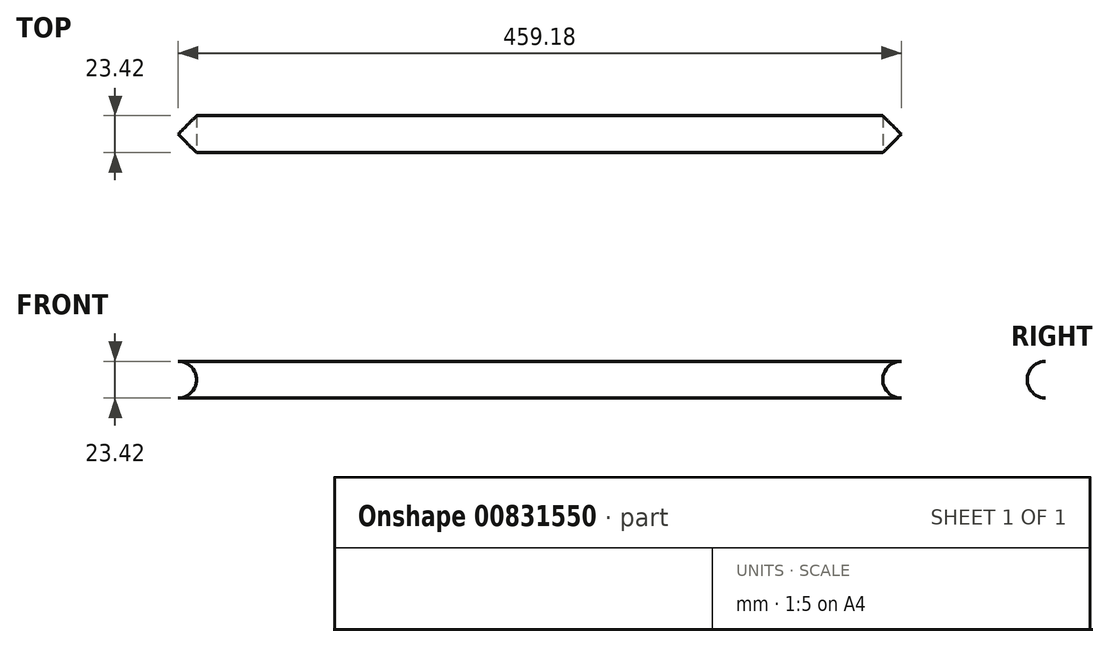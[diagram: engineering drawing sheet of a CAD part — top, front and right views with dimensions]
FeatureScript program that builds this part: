
annotation { "Feature Type Name" : "Feature", "Feature Type Description" : "" }
export const myFeature = defineFeature(function(context is Context, id is Id, definition is map)
    precondition{}
    {
        {
            var Q0;
            Q0=qCreatedBy(makeId("Right.planeOp"),FACE);
            var sketch = newSketch(context, id + "F0", { "sketchPlane" : qUnion([Q0])});
            skCircle(sketch, "E0", {"center": v(0, 0) * mm, "radius": 11.7 * mm});
            skSolve(sketch);
        }
        {
            var Q0;
            Q0=makeQuery(id+"F0.imprint","IMPRINT",FACE,{"disambiguationData":[TD([[makeQuery(id+"F0.imprint","IMPRINT",EDGE,{"derivedFrom":sQuery(id+"F0.wireOp",EDGE,"E0")}),1.0]])]});
            extrude(context, id + "F1", {"entities" : qUnion([Q0]), "depth" : 459.18 * mm, "offsetDistance" : 25.4 * mm});
        }
        {
            var Q0;
            Q0=qCreatedBy(makeId("Front.planeOp"),FACE);
            var sketch = newSketch(context, id + "F2", { "sketchPlane" : qUnion([Q0])});
            skCircle(sketch, "E1", {"center": v(0, 0) * mm, "radius": 11.7 * mm});
            skCircle(sketch, "E2", {"center": v(459.18, 0) * mm, "radius": 11.7 * mm});
            skSolve(sketch);
        }
        {
            var Q0;
            Q0=makeQuery(id+"F2.imprint","IMPRINT",FACE,{"disambiguationData":[TD([[makeQuery(id+"F2.imprint","IMPRINT",EDGE,{"derivedFrom":sQuery(id+"F2.wireOp",EDGE,"E1")}),1.0]])]});
            var Q1;
            Q1=makeQuery(id+"F2.imprint","IMPRINT",FACE,{"disambiguationData":[TD([[makeQuery(id+"F2.imprint","IMPRINT",EDGE,{"derivedFrom":sQuery(id+"F2.wireOp",EDGE,"E2")}),1.0]])]});
            extrude(context, id + "F3", {"entities" : qUnion([Q0, Q1]), "operationType" : NewBodyOperationType.REMOVE, "endBound" : BoundingType.THROUGH_ALL, "oppositeDirection" : true, "depth" : 25.4 * mm, "offsetDistance" : 25.4 * mm, "hasSecondDirection" : true, "secondDirectionBound" : SecondDirectionBoundingType.THROUGH_ALL, "secondDirectionOppositeDirection" : false, "secondDirectionDepth" : 25.4 * mm});
        }
    });
